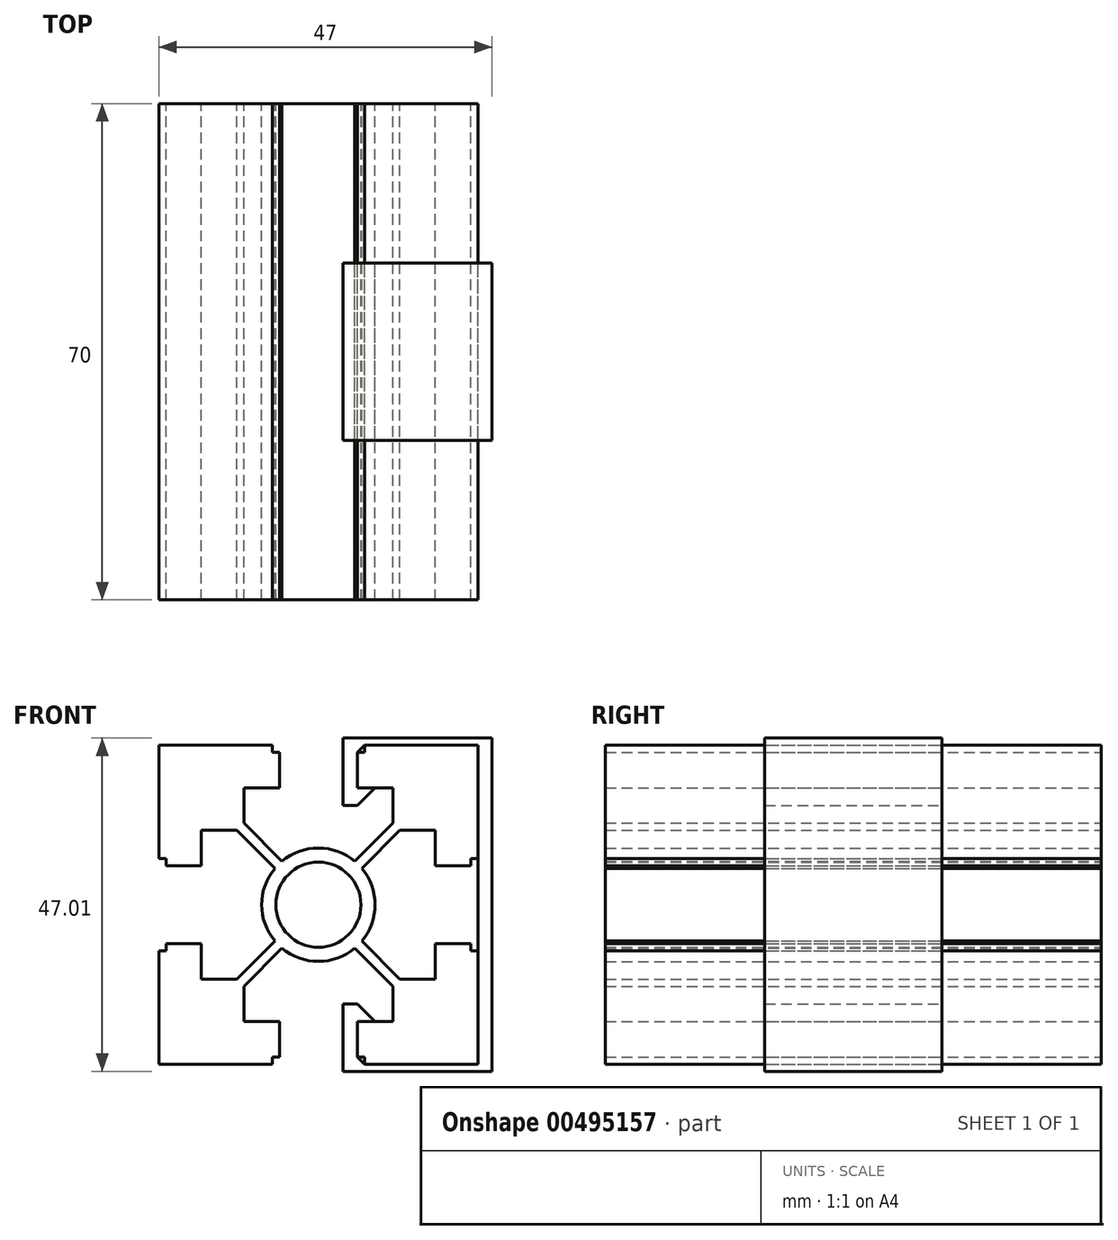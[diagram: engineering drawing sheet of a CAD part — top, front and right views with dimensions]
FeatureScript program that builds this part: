
annotation { "Feature Type Name" : "Feature", "Feature Type Description" : "" }
export const myFeature = defineFeature(function(context is Context, id is Id, definition is map)
    precondition{}
    {
        {
            var Q0;
            Q0=qCreatedBy(makeId("Front.planeOp"),FACE);
            var sketch = newSketch(context, id + "F0", { "sketchPlane" : qUnion([Q0])});
            skPoint(sketch, "E0.middle", {"position": v(0, 0) * mm});
            skPoint(sketch, "E1", {"position": v(-6.5, 22.5) * mm});
            skLineSegment(sketch, "E2", {"start": v(-6.5, 22.5) * mm, "end": v(-6.5, 21.5) * mm});
            skLineSegment(sketch, "E3", {"start": v(-6.5, 21.5) * mm, "end": v(-5.5, 21.5) * mm});
            skLineSegment(sketch, "E4", {"start": v(-5.5, 21.5) * mm, "end": v(-5.5, 16.5) * mm});
            skLineSegment(sketch, "E5", {"start": v(-5.5, 16.5) * mm, "end": v(-10.5, 16.5) * mm});
            skLineSegment(sketch, "E6", {"start": v(-10.5, 16.5) * mm, "end": v(-10.5, 11.5) * mm});
            skCircle(sketch, "E7", {"center": v(0, 0) * mm, "radius": 8 * mm});
            skLineSegment(sketch, "E8", {"start": v(-22.5, 22.5) * mm, "end": v(-6.5, 22.5) * mm});
            skLineSegment(sketch, "E9", {"start": v(22.5, 22.5) * mm, "end": v(6.5, 22.5) * mm});
            skLineSegment(sketch, "E10", {"start": v(6.5, 22.5) * mm, "end": v(6.5, 21.5) * mm});
            skLineSegment(sketch, "E11", {"start": v(6.5, 21.5) * mm, "end": v(5.5, 21.5) * mm});
            skLineSegment(sketch, "E12", {"start": v(5.5, 21.5) * mm, "end": v(5.5, 16.5) * mm});
            skLineSegment(sketch, "E13", {"start": v(5.5, 16.5) * mm, "end": v(10.5, 16.5) * mm});
            skLineSegment(sketch, "E14", {"start": v(10.5, 16.5) * mm, "end": v(10.5, 11.5) * mm});
            skPoint(sketch, "E15", {"position": v(-22.5, 6.5) * mm});
            skLineSegment(sketch, "E16", {"start": v(-22.5, 6.5) * mm, "end": v(-22.5, 22.5) * mm});
            skLineSegment(sketch, "E17", {"start": v(-22.5, 6.5) * mm, "end": v(-21.5, 6.5) * mm});
            skLineSegment(sketch, "E18", {"start": v(-21.5, 6.5) * mm, "end": v(-21.5, 5.5) * mm});
            skLineSegment(sketch, "E19", {"start": v(-21.5, 5.5) * mm, "end": v(-16.5, 5.5) * mm});
            skLineSegment(sketch, "E20", {"start": v(-16.5, 5.5) * mm, "end": v(-16.5, 10.5) * mm});
            skLineSegment(sketch, "E21", {"start": v(-16.5, 10.5) * mm, "end": v(-11.5, 10.5) * mm});
            skLineSegment(sketch, "E22", {"start": v(-22.5, -22.5) * mm, "end": v(-22.5, -6.5) * mm});
            skLineSegment(sketch, "E23", {"start": v(-22.5, -6.5) * mm, "end": v(-21.5, -6.5) * mm});
            skLineSegment(sketch, "E24", {"start": v(-21.5, -6.5) * mm, "end": v(-21.5, -5.5) * mm});
            skLineSegment(sketch, "E25", {"start": v(-21.5, -5.5) * mm, "end": v(-16.5, -5.5) * mm});
            skLineSegment(sketch, "E26", {"start": v(-16.5, -5.5) * mm, "end": v(-16.5, -10.5) * mm});
            skLineSegment(sketch, "E27", {"start": v(-16.5, -10.5) * mm, "end": v(-11.5, -10.5) * mm});
            skLineSegment(sketch, "E28", {"start": v(-22.5, -22.5) * mm, "end": v(-6.5, -22.5) * mm});
            skLineSegment(sketch, "E29", {"start": v(-6.5, -22.5) * mm, "end": v(-6.5, -21.5) * mm});
            skLineSegment(sketch, "E30", {"start": v(-6.5, -21.5) * mm, "end": v(-5.5, -21.5) * mm});
            skLineSegment(sketch, "E31", {"start": v(-5.5, -21.5) * mm, "end": v(-5.5, -16.5) * mm});
            skLineSegment(sketch, "E32", {"start": v(-5.5, -16.5) * mm, "end": v(-10.5, -16.5) * mm});
            skLineSegment(sketch, "E33", {"start": v(-10.5, -16.5) * mm, "end": v(-10.5, -11.5) * mm});
            skLineSegment(sketch, "E34", {"start": v(22.5, -22.5) * mm, "end": v(6.5, -22.5) * mm});
            skLineSegment(sketch, "E35", {"start": v(6.5, -22.5) * mm, "end": v(6.5, -21.5) * mm});
            skLineSegment(sketch, "E36", {"start": v(6.5, -21.5) * mm, "end": v(5.5, -21.5) * mm});
            skLineSegment(sketch, "E37", {"start": v(5.5, -21.5) * mm, "end": v(5.5, -16.5) * mm});
            skLineSegment(sketch, "E38", {"start": v(5.5, -16.5) * mm, "end": v(10.5, -16.5) * mm});
            skLineSegment(sketch, "E39", {"start": v(10.5, -16.5) * mm, "end": v(10.5, -11.5) * mm});
            skLineSegment(sketch, "E40", {"start": v(22.5, -22.5) * mm, "end": v(22.5, -6.5) * mm});
            skLineSegment(sketch, "E41", {"start": v(22.5, -6.5) * mm, "end": v(21.5, -6.5) * mm});
            skLineSegment(sketch, "E42", {"start": v(21.5, -6.5) * mm, "end": v(21.5, -5.5) * mm});
            skLineSegment(sketch, "E43", {"start": v(21.5, -5.5) * mm, "end": v(16.5, -5.5) * mm});
            skLineSegment(sketch, "E44", {"start": v(16.5, -5.5) * mm, "end": v(16.5, -10.5) * mm});
            skLineSegment(sketch, "E45", {"start": v(16.5, -10.5) * mm, "end": v(11.5, -10.5) * mm});
            skLineSegment(sketch, "E46", {"start": v(22.5, 22.5) * mm, "end": v(22.5, 6.5) * mm});
            skLineSegment(sketch, "E47", {"start": v(22.5, 6.5) * mm, "end": v(21.5, 6.5) * mm});
            skLineSegment(sketch, "E48", {"start": v(21.5, 6.5) * mm, "end": v(21.5, 5.5) * mm});
            skLineSegment(sketch, "E49", {"start": v(21.5, 5.5) * mm, "end": v(16.5, 5.5) * mm});
            skLineSegment(sketch, "E50", {"start": v(16.5, 5.5) * mm, "end": v(16.5, 10.5) * mm});
            skLineSegment(sketch, "E51", {"start": v(16.5, 10.5) * mm, "end": v(11.5, 10.5) * mm});
            skPoint(sketch, "E52", {"position": v(-5.13, 6.13) * mm});
            skPoint(sketch, "E53", {"position": v(-6.13, 5.13) * mm});
            skPoint(sketch, "E54", {"position": v(5.13, -6.13) * mm});
            skPoint(sketch, "E55", {"position": v(6.13, -5.13) * mm});
            skPoint(sketch, "E56", {"position": v(5.13, 6.13) * mm});
            skPoint(sketch, "E57", {"position": v(6.13, 5.13) * mm});
            skPoint(sketch, "E58", {"position": v(-6.13, -5.13) * mm});
            skPoint(sketch, "E59", {"position": v(-5.13, -6.13) * mm});
            skLineSegment(sketch, "E60", {"start": v(-10.5, 11.5) * mm, "end": v(-5.13, 6.13) * mm});
            skLineSegment(sketch, "E61", {"start": v(-11.5, 10.5) * mm, "end": v(-6.13, 5.13) * mm});
            skLineSegment(sketch, "E62", {"start": v(5.13, 6.13) * mm, "end": v(10.5, 11.5) * mm});
            skLineSegment(sketch, "E63", {"start": v(6.13, 5.13) * mm, "end": v(11.5, 10.5) * mm});
            skLineSegment(sketch, "E64", {"start": v(6.13, -5.13) * mm, "end": v(11.5, -10.5) * mm});
            skLineSegment(sketch, "E65", {"start": v(5.13, -6.13) * mm, "end": v(10.5, -11.5) * mm});
            skLineSegment(sketch, "E66", {"start": v(-5.13, -6.13) * mm, "end": v(-10.5, -11.5) * mm});
            skLineSegment(sketch, "E67", {"start": v(-11.5, -10.5) * mm, "end": v(-6.13, -5.13) * mm});
            skCircle(sketch, "E68", {"center": v(0, 0) * mm, "radius": 6 * mm});
            skSolve(sketch);
        }
        {
            var Q0;
            Q0=qSketchRegion(id+"F0",true);
            extrude(context, id + "F1", {"entities" : qUnion([Q0]), "depth" : 70 * mm, "symmetric" : true});
        }
        {
            var Q0;
            Q0=qCreatedBy(makeId("Front.planeOp"),FACE);
            var sketch = newSketch(context, id + "F2", { "sketchPlane" : qUnion([Q0])});
            skPoint(sketch, "E69", {"position": v(5.5, 16.5) * mm});
            skPoint(sketch, "E70", {"position": v(8, 16.5) * mm});
            skPoint(sketch, "E71", {"position": v(5.5, 21.5) * mm});
            skPoint(sketch, "E72", {"position": v(6.5, 22.5) * mm});
            skPoint(sketch, "E73", {"position": v(22.5, 22.5) * mm});
            skPoint(sketch, "E74", {"position": v(22.5, -22.5) * mm});
            skPoint(sketch, "E75", {"position": v(6.5, -22.5) * mm});
            skPoint(sketch, "E76", {"position": v(5.5, -21.5) * mm});
            skPoint(sketch, "E77", {"position": v(5.5, -16.5) * mm});
            skPoint(sketch, "E78", {"position": v(8, -16.5) * mm});
            skLineSegment(sketch, "E79", {"start": v(8, 16.5) * mm, "end": v(5.5, 16.5) * mm});
            skLineSegment(sketch, "E80", {"start": v(5.5, 21.5) * mm, "end": v(6.5, 22.5) * mm});
            skLineSegment(sketch, "E81", {"start": v(5.5, 21.5) * mm, "end": v(5.5, 16.5) * mm});
            skLineSegment(sketch, "E82", {"start": v(6.5, 22.5) * mm, "end": v(22.5, 22.5) * mm});
            skLineSegment(sketch, "E83", {"start": v(22.5, 22.5) * mm, "end": v(22.5, -22.5) * mm});
            skLineSegment(sketch, "E84", {"start": v(22.5, -22.5) * mm, "end": v(6.5, -22.5) * mm});
            skLineSegment(sketch, "E85", {"start": v(6.5, -22.5) * mm, "end": v(5.5, -21.5) * mm});
            skLineSegment(sketch, "E86", {"start": v(5.5, -21.5) * mm, "end": v(5.5, -16.5) * mm});
            skLineSegment(sketch, "E87", {"start": v(5.5, -16.5) * mm, "end": v(8, -16.5) * mm});
            skLineSegment(sketch, "E88", {"start": v(8, -16.5) * mm, "end": v(5.5, -14) * mm});
            skLineSegment(sketch, "E89", {"start": v(5.5, -14) * mm, "end": v(3.5, -14) * mm});
            skLineSegment(sketch, "E90", {"start": v(3.46, -23.5) * mm, "end": v(3.5, -14) * mm});
            skLineSegment(sketch, "E91", {"start": v(8, 16.5) * mm, "end": v(5.5, 14) * mm});
            skLineSegment(sketch, "E92", {"start": v(3.5, 14) * mm, "end": v(5.5, 14) * mm});
            skLineSegment(sketch, "E93", {"start": v(3.5, 23.5) * mm, "end": v(3.5, 14) * mm});
            skLineSegment(sketch, "E94", {"start": v(3.5, 23.5) * mm, "end": v(24.5, 23.5) * mm});
            skLineSegment(sketch, "E95", {"start": v(24.5, 23.5) * mm, "end": v(24.5, -23.5) * mm});
            skLineSegment(sketch, "E96", {"start": v(3.46, -23.5) * mm, "end": v(24.5, -23.5) * mm});
            skSolve(sketch);
        }
        {
            var Q0;
            Q0=qSketchRegion(id+"F2",true);
            extrude(context, id + "F3", {"entities" : qUnion([Q0]), "depth" : 25 * mm, "symmetric" : true});
        }
    });
